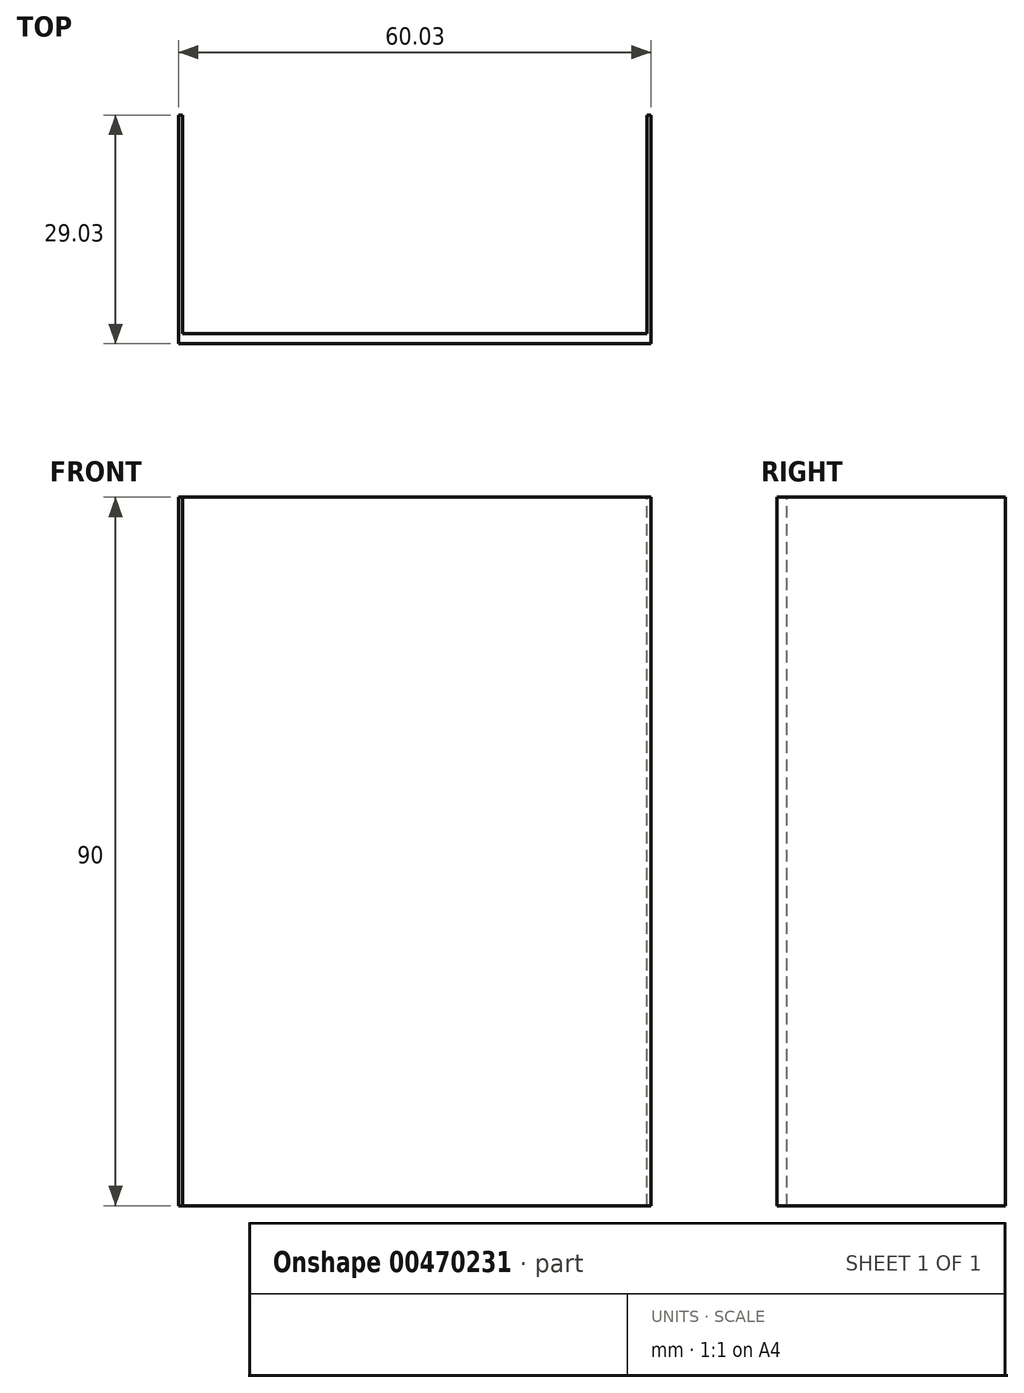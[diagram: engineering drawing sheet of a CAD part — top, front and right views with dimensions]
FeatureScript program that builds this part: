
annotation { "Feature Type Name" : "Feature", "Feature Type Description" : "" }
export const myFeature = defineFeature(function(context is Context, id is Id, definition is map)
    precondition{}
    {
        {
            var Q0;
            Q0=qCreatedBy(makeId("Top.planeOp"),FACE);
            var sketch = newSketch(context, id + "F0", { "sketchPlane" : qUnion([Q0])});
            skLineSegment(sketch, "E0.bottom", {"start": v(30.94, 15) * mm, "end": v(-28.06, 15) * mm});
            skLineSegment(sketch, "E0.top", {"start": v(30.94, 13.73) * mm, "end": v(-28.06, 13.73) * mm});
            skLineSegment(sketch, "E0.left", {"start": v(30.94, 15) * mm, "end": v(30.94, 13.73) * mm});
            skLineSegment(sketch, "E0.right", {"start": v(-28.06, 15) * mm, "end": v(-28.06, 13.73) * mm});
            skSolve(sketch);
        }
        {
            var Q0;
            Q0=makeQuery(id+"F0.imprint","IMPRINT",FACE,{"disambiguationData":[TD([[makeQuery(id+"F0.imprint","IMPRINT",EDGE,{"derivedFrom":sQuery(id+"F0.wireOp",EDGE,"E0.bottom")}),1.0]])]});
            extrude(context, id + "F1", {"entities" : qUnion([Q0]), "oppositeDirection" : true, "depth" : 90 * mm});
        }
        {
            var Q0;
            Q0=qCreatedBy(makeId("Top.planeOp"),FACE);
            var sketch = newSketch(context, id + "F2", { "sketchPlane" : qUnion([Q0])});
            skLineSegment(sketch, "E1.bottom", {"start": v(-28.58, 28.25) * mm, "end": v(-28.06, 28.25) * mm});
            skLineSegment(sketch, "E1.top", {"start": v(-28.58, 13.75) * mm, "end": v(-28.06, 13.75) * mm});
            skLineSegment(sketch, "E1.left", {"start": v(-28.58, 28.25) * mm, "end": v(-28.58, 13.75) * mm});
            skLineSegment(sketch, "E1.right", {"start": v(-28.06, 28.25) * mm, "end": v(-28.06, 13.75) * mm});
            skLineSegment(sketch, "E2.bottom", {"start": v(30.93, 28.23) * mm, "end": v(31.45, 28.23) * mm});
            skLineSegment(sketch, "E2.top", {"start": v(30.93, 13.73) * mm, "end": v(31.45, 13.73) * mm});
            skLineSegment(sketch, "E2.left", {"start": v(30.93, 28.23) * mm, "end": v(30.93, 13.73) * mm});
            skLineSegment(sketch, "E2.right", {"start": v(31.45, 28.23) * mm, "end": v(31.45, 13.73) * mm});
            skLineSegment(sketch, "E3.bottom", {"start": v(-28.58, 42.76) * mm, "end": v(-28.06, 42.76) * mm});
            skLineSegment(sketch, "E3.left", {"start": v(-28.58, 42.76) * mm, "end": v(-28.58, 28.25) * mm});
            skLineSegment(sketch, "E3.right", {"start": v(-28.06, 42.76) * mm, "end": v(-28.06, 28.25) * mm});
            skLineSegment(sketch, "E4.bottom", {"start": v(30.93, 42.74) * mm, "end": v(31.45, 42.74) * mm});
            skLineSegment(sketch, "E4.left", {"start": v(30.93, 42.74) * mm, "end": v(30.93, 28.23) * mm});
            skLineSegment(sketch, "E4.right", {"start": v(31.45, 42.74) * mm, "end": v(31.45, 28.23) * mm});
            skSolve(sketch);
        }
        {
            var Q0;
            Q0=makeQuery(id+"F2.imprint","IMPRINT",FACE,{"disambiguationData":[TD([[makeQuery(id+"F2.imprint","IMPRINT",EDGE,{"derivedFrom":sQuery(id+"F2.wireOp",EDGE,"E1.bottom")}),-1.0]])]});
            extrude(context, id + "F3", {"entities" : qUnion([Q0]), "operationType" : NewBodyOperationType.ADD, "oppositeDirection" : true, "depth" : 90 * mm});
        }
        {
            var Q0;
            Q0 = qSketchRegion(id + "F2", true);
            extrude(context, id + "F4", {"entities" : qUnion([Q0]), "operationType" : NewBodyOperationType.ADD, "oppositeDirection" : true, "depth" : 90 * mm});
        }
        {
            var Q0;
            Q0=qCreatedBy(makeId("Right.planeOp"),FACE);
            var sketch = newSketch(context, id + "F5", { "sketchPlane" : qUnion([Q0])});
            skLineSegment(sketch, "E5.bottom", {"start": v(13.66, 0.98) * mm, "end": v(42.78, 0.98) * mm});
            skLineSegment(sketch, "E5.top", {"start": v(13.66, 0) * mm, "end": v(42.78, 0) * mm});
            skLineSegment(sketch, "E5.left", {"start": v(13.66, 0.98) * mm, "end": v(13.66, 0) * mm});
            skLineSegment(sketch, "E5.right", {"start": v(42.78, 0.98) * mm, "end": v(42.78, 0) * mm});
            skSolve(sketch);
        }
        {
            var Q0;
            Q0=sQuery(id+"F5.wireOp",EDGE,"E5.top");
            extrude(context, id + "F6", {"bodyType" : ToolBodyType.SURFACE, "surfaceEntities" : qUnion([Q0]), "depth" : 31.75 * mm, "hasSecondDirection" : true, "secondDirectionOppositeDirection" : true, "secondDirectionDepth" : 28.7 * mm});
        }
    });
